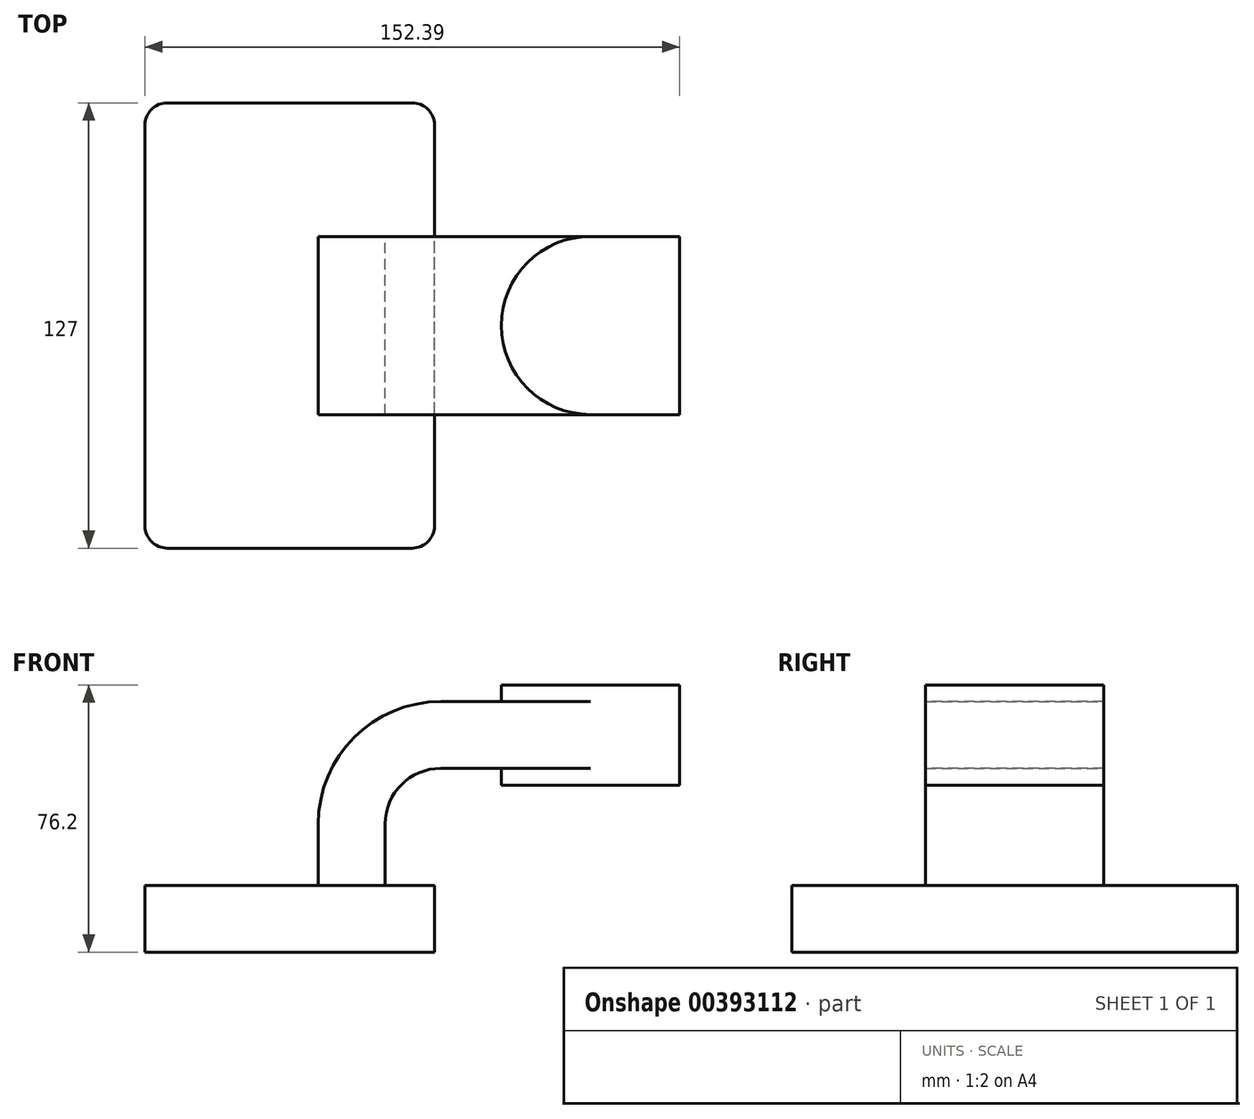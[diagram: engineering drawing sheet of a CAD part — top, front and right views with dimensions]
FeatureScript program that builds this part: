
annotation { "Feature Type Name" : "Feature", "Feature Type Description" : "" }
export const myFeature = defineFeature(function(context is Context, id is Id, definition is map)
    precondition{}
    {
        {
            var Q0;
            Q0=qCreatedBy(makeId("Front.planeOp"),FACE);
            var sketch = newSketch(context, id + "F0", { "sketchPlane" : qUnion([Q0])});
            skLineSegment(sketch, "E0.bottom", {"start": v(-41.28, 9.53) * mm, "end": v(41.28, 9.53) * mm});
            skLineSegment(sketch, "E0.top", {"start": v(-41.28, -9.53) * mm, "end": v(41.28, -9.53) * mm});
            skLineSegment(sketch, "E0.left", {"start": v(-41.28, 9.53) * mm, "end": v(-41.28, -9.53) * mm});
            skLineSegment(sketch, "E0.right", {"start": v(41.28, 9.53) * mm, "end": v(41.28, -9.53) * mm});
            skPoint(sketch, "E0.middle", {"position": v(0, 0) * mm});
            skLineSegment(sketch, "E1.bottom", {"start": v(60.33, 66.68) * mm, "end": v(111.13, 66.68) * mm});
            skLineSegment(sketch, "E1.top", {"start": v(60.33, 38.1) * mm, "end": v(111.13, 38.1) * mm});
            skLineSegment(sketch, "E1.left", {"start": v(60.33, 66.68) * mm, "end": v(60.33, 38.1) * mm});
            skLineSegment(sketch, "E1.right", {"start": v(111.13, 66.68) * mm, "end": v(111.13, 38.1) * mm});
            skPoint(sketch, "E1.middle", {"position": v(85.73, 52.39) * mm});
            skLineSegment(sketch, "E2", {"start": v(27.18, 9.53) * mm, "end": v(27.18, 27) * mm});
            skArc(sketch, "E3", {"start": v(27.18, 27) * mm, "mid": v(31.83, 38.23) * mm, "end": v(43.06, 42.88) * mm});
            skLineSegment(sketch, "E4", {"start": v(43.06, 42.88) * mm, "end": v(85.73, 42.88) * mm});
            skArc(sketch, "E5.1", {"start": v(8.13, 27) * mm, "mid": v(18.36, 51.7) * mm, "end": v(43.06, 61.93) * mm});
            skLineSegment(sketch, "E6", {"start": v(8.13, 27) * mm, "end": v(8.13, 9.53) * mm});
            skLineSegment(sketch, "E7", {"start": v(85.73, 38.1) * mm, "end": v(85.73, 66.68) * mm});
            skLineSegment(sketch, "E8", {"start": v(43.06, 61.93) * mm, "end": v(85.73, 61.93) * mm});
            skFitSpline(sketch, "E9", {"points": [v(-41.28, 9.53) * mm, v(43.06, 61.93) * mm], "startDerivative": vector(1.3, 91.31) * mm, "endDerivative": vector(56.47, -3.84) * mm});
            skSolve(sketch);
        }
        {
            var Q0;
            Q0=makeQuery(id+"F0.imprint","IMPRINT",FACE,{"disambiguationData":[TD([[makeQuery(id+"F0.imprint","IMPRINT",EDGE,{"derivedFrom":sQuery(id+"F0.wireOp",EDGE,"E0.top")}),1.0]])]});
            extrude(context, id + "F1", {"entities" : qUnion([Q0]), "endBound" : BoundingType.SYMMETRIC, "depth" : 127 * mm});
        }
        {
            var Q0;
            {var subQ1=sQuery(id+"F0.wireOp",EDGE,"E2");Q0=makeQuery(id+"F0.imprint","IMPRINT",FACE,{"disambiguationData":[TD([[makeQuery(id+"F0.imprint","IMPRINT",EDGE,{"derivedFrom":subQ1}),1.0]])]});}
            var Q1;
            {var subQ4=sQuery(id+"F0.wireOp",EDGE,"E1.right");Q1=makeQuery(id+"F0.imprint","IMPRINT",FACE,{"disambiguationData":[TD([[makeQuery(id+"F0.imprint","IMPRINT",EDGE,{"derivedFrom":subQ4}),-1.0]])]});}
            var Q2;
            {var subQ0=sQuery(id+"F0.wireOp",EDGE,"E8");var subQ1=sQuery(id+"F0.wireOp",EDGE,"E1.left");var subQ2=makeQuery(id+"F0.imprint","INTERSECT",VERTEX,{"derivedFrom":[subQ1,subQ0]});Q2=makeQuery(id+"F0.imprint","IMPRINT",FACE,{"disambiguationData":[TD([[makeQuery(id+"F0.imprint","IMPRINT",EDGE,{"disambiguationData":[TD([[subQ2,-1.0]])],"derivedFrom":subQ1}),1.0]])]});}
            extrude(context, id + "F2", {"entities" : qUnion([Q0, Q1, Q2]), "operationType" : NewBodyOperationType.ADD, "endBound" : BoundingType.SYMMETRIC, "depth" : 50.8 * mm});
        }
        {
            var Q0;
            Q0=makeQuery(id+"F0.imprint","IMPRINT",FACE,{"disambiguationData":[TD([[makeQuery(id+"F0.imprint","IMPRINT",EDGE,{"derivedFrom":sQuery(id+"F0.wireOp",EDGE,"E5.1")}),1.0]])]});
            extrude(context, id + "F3", {"entities" : qUnion([Q0]), "operationType" : NewBodyOperationType.ADD, "endBound" : BoundingType.SYMMETRIC, "depth" : 15.88 * mm});
        }
        {
            var Q0;
            {var subQ4=sQuery(id+"F0.wireOp",EDGE,"E1.right");Q0=makeQuery(id+"F0.imprint","IMPRINT",FACE,{"disambiguationData":[TD([[makeQuery(id+"F0.imprint","IMPRINT",EDGE,{"derivedFrom":subQ4}),-1.0]])]});}
            var Q1;
            Q1=sQuery(id+"F0.wireOp",EDGE,"E7");
            revolve(context, id + "F4", {"operationType" : NewBodyOperationType.ADD, "entities" : qUnion([Q0]), "axis" : qUnion([Q1]), "revolveType" : RevolveType.FULL});
        }
        {
            var Q0;
            Q0=makeQuery(id+"F1.opExtrude","CAP_EDGE",EDGE,{"disambiguationData":[OSD([sQuery(id+"F0.wireOp",EDGE,"E0.left")])],"isStart":false});
            var Q1;
            Q1=makeQuery(id+"F1.opExtrude","CAP_EDGE",EDGE,{"disambiguationData":[OSD([sQuery(id+"F0.wireOp",EDGE,"E0.right")])],"isStart":false});
            var Q2;
            Q2=makeQuery(id+"F1.opExtrude","CAP_EDGE",EDGE,{"disambiguationData":[OSD([sQuery(id+"F0.wireOp",EDGE,"E0.right")])],"isStart":true});
            var Q3;
            Q3=makeQuery(id+"F1.opExtrude","CAP_EDGE",EDGE,{"disambiguationData":[OSD([sQuery(id+"F0.wireOp",EDGE,"E0.left")])],"isStart":true});
            fillet(context, id + "F5", {"entities" : qUnion([Q0, Q1, Q2, Q3]), "radius" : 6.35 * mm, "tangentPropagation" : true, "allowEdgeOverflow" : false});
        }
    });
